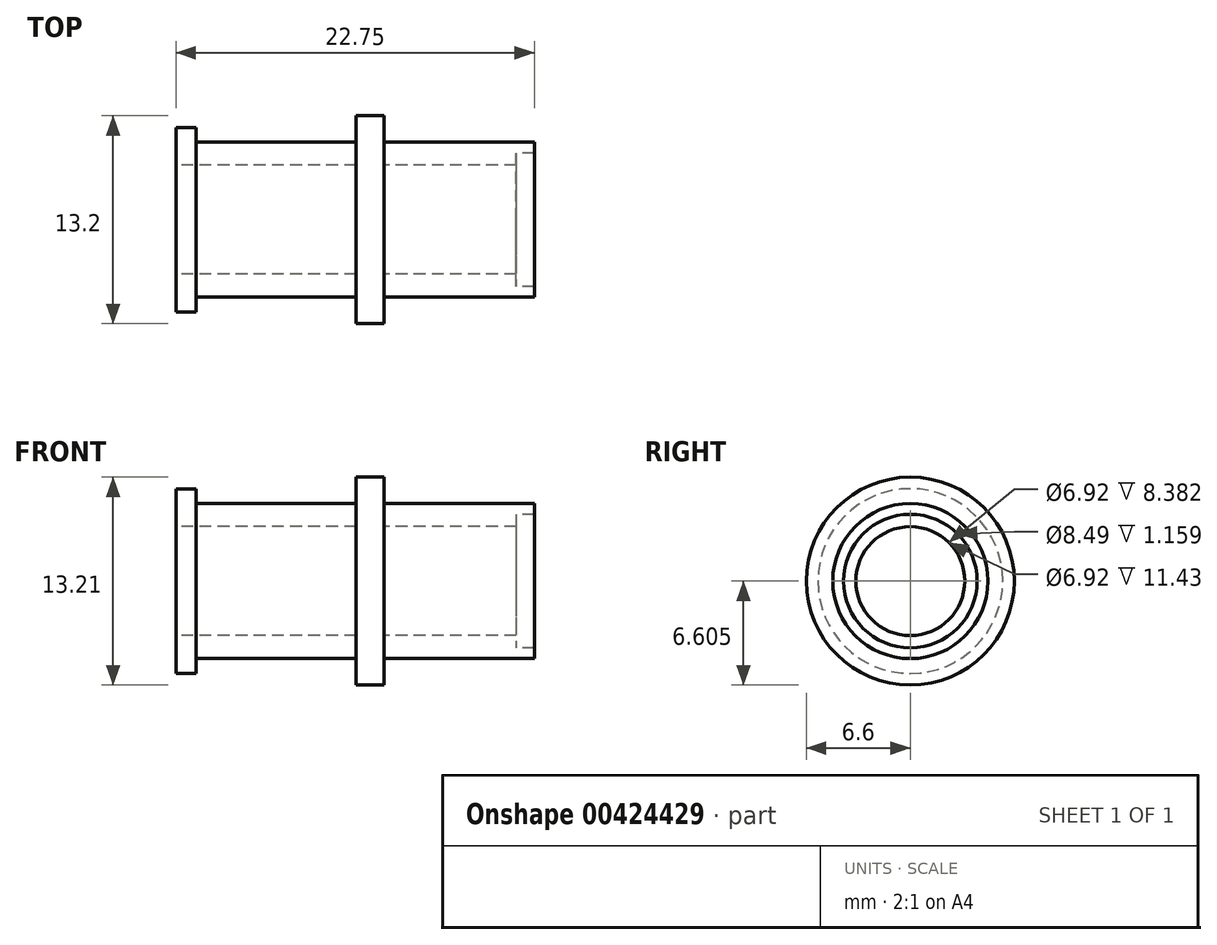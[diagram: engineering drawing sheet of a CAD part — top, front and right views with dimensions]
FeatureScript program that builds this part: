
annotation { "Feature Type Name" : "Feature", "Feature Type Description" : "" }
export const myFeature = defineFeature(function(context is Context, id is Id, definition is map)
    precondition{}
    {
        {
            var Q0;
            Q0=qCreatedBy(makeId("Front.planeOp"),FACE);
            var sketch = newSketch(context, id + "F0", { "sketchPlane" : qUnion([Q0])});
            skLineSegment(sketch, "E0", {"start": v(0, 0) * mm, "end": v(0, 2.25) * mm});
            skLineSegment(sketch, "E1", {"start": v(8.38, 2.25) * mm, "end": v(8.38, 3.04) * mm});
            skLineSegment(sketch, "E2", {"start": v(9.54, 3.04) * mm, "end": v(9.54, 3.72) * mm});
            skLineSegment(sketch, "E3", {"start": v(9.54, 3.72) * mm, "end": v(0, 3.72) * mm});
            skLineSegment(sketch, "E4", {"start": v(0, 3.72) * mm, "end": v(0, 5.4) * mm});
            skLineSegment(sketch, "E5", {"start": v(0, 5.4) * mm, "end": v(-1.78, 5.4) * mm});
            skLineSegment(sketch, "E6", {"start": v(-1.78, 5.4) * mm, "end": v(-1.78, 3.72) * mm});
            skLineSegment(sketch, "E7", {"start": v(-1.78, 3.72) * mm, "end": v(-11.94, 3.72) * mm});
            skLineSegment(sketch, "E8", {"start": v(-11.94, 3.72) * mm, "end": v(-11.94, 4.66) * mm});
            skLineSegment(sketch, "E9", {"start": v(-11.94, 4.66) * mm, "end": v(-13.2, 4.66) * mm});
            skLineSegment(sketch, "E10", {"start": v(-13.2, 4.66) * mm, "end": v(-13.2, 2.25) * mm});
            skLineSegment(sketch, "E11", {"start": v(-13.2, 2.25) * mm, "end": v(-1.78, 2.25) * mm});
            skLineSegment(sketch, "E12", {"start": v(-1.78, 2.25) * mm, "end": v(-1.78, -1.2) * mm});
            skLineSegment(sketch, "E13", {"start": v(-1.78, -1.2) * mm, "end": v(0, -1.2) * mm});
            skLineSegment(sketch, "E14", {"start": v(9.54, 3.04) * mm, "end": v(8.38, 3.04) * mm});
            skLineSegment(sketch, "E15", {"start": v(0, 2.25) * mm, "end": v(8.38, 2.25) * mm});
            skLineSegment(sketch, "E16", {"start": v(0, -1.2) * mm, "end": v(0, 0.42) * mm});
            skSolve(sketch);
        }
        {
            var Q0;
            {var subQ0=sQuery(id+"F0.wireOp",EDGE,"E0");Q0=makeQuery(id+"F0.imprint","IMPRINT",FACE,{"disambiguationData":[TD([[makeQuery(id+"F0.imprint","IMPRINT",EDGE,{"derivedFrom":subQ0}),1.0]])]});}
            var Q1;
            Q1=sQuery(id+"F0.wireOp",EDGE,"E13");
            revolve(context, id + "F1", {"entities" : qUnion([Q0]), "axis" : qUnion([Q1]), "revolveType" : RevolveType.FULL});
        }
    });
